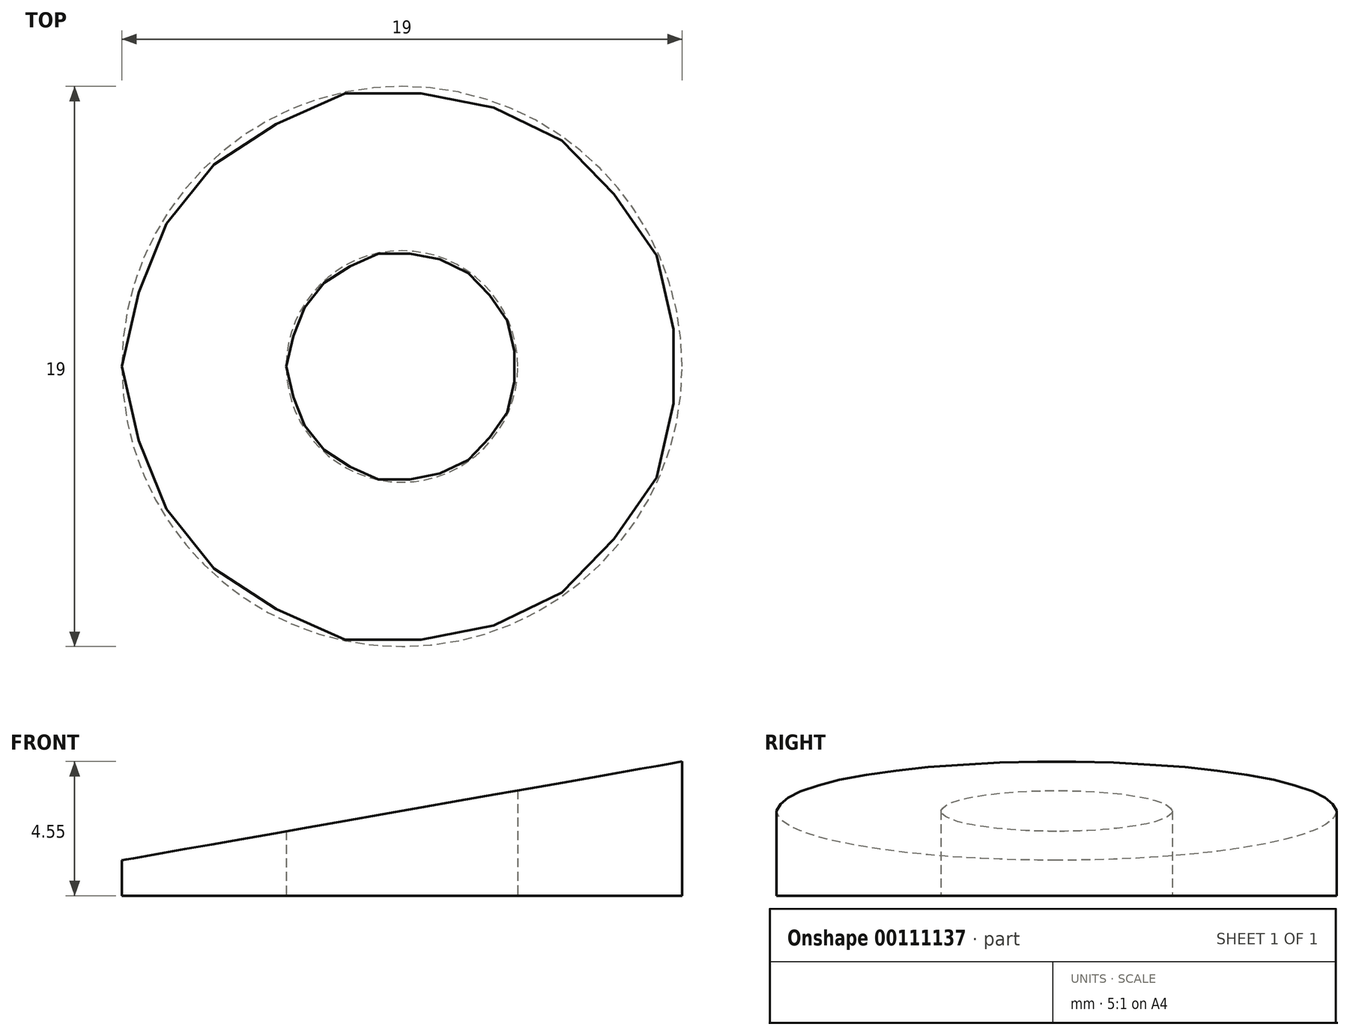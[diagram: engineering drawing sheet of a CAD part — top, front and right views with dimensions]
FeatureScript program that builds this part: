
annotation { "Feature Type Name" : "Feature", "Feature Type Description" : "" }
export const myFeature = defineFeature(function(context is Context, id is Id, definition is map)
    precondition{}
    {
        {
            var Q0;
            Q0=qCreatedBy(makeId("Top.planeOp"),FACE);
            var sketch = newSketch(context, id + "F0", { "sketchPlane" : qUnion([Q0])});
            skCircle(sketch, "E0", {"center": v(0, 0) * mm, "radius": 3.93 * mm});
            skCircle(sketch, "E1", {"center": v(0, 0) * mm, "radius": 9.5 * mm});
            skSolve(sketch);
        }
        {
            var Q0;
            Q0 = qSketchRegion(id + "F0", true);
            extrude(context, id + "F1", {"entities" : qUnion([Q0]), "depth" : 6 * mm, "offsetDistance" : 25 * mm});
        }
        {
            var Q0;
            Q0=qCreatedBy(makeId("Front.planeOp"),FACE);
            var sketch = newSketch(context, id + "F2", { "sketchPlane" : qUnion([Q0])});
            skLineSegment(sketch, "E2.0", {"start": v(-9.5, 0) * mm, "end": v(9.5, 0) * mm});
            skLineSegment(sketch, "E3.0", {"start": v(-9.5, 6) * mm, "end": v(9.5, 6) * mm, "construction": true});
            skLineSegment(sketch, "E4", {"start": v(-9.5, 0) * mm, "end": v(-9.5, 6) * mm, "construction": true});
            skLineSegment(sketch, "E5", {"start": v(9.5, 6) * mm, "end": v(9.5, 0) * mm});
            skLineSegment(sketch, "E6", {"start": v(-9.5, 1.2) * mm, "end": v(9.5, 4.55) * mm});
            skLineSegment(sketch, "E7", {"start": v(-9.5, 1.2) * mm, "end": v(-9.5, 0) * mm});
            skSolve(sketch);
        }
        {
            var Q0;
            {var subQ0=sQuery(id+"F2.wireOp",EDGE,"E2.0");Q0=makeQuery(id+"F2.imprint","IMPRINT",FACE,{"disambiguationData":[TD([[makeQuery(id+"F2.imprint","IMPRINT",EDGE,{"derivedFrom":subQ0}),1.0]])]});}
            extrude(context, id + "F3", {"entities" : qUnion([Q0]), "operationType" : NewBodyOperationType.INTERSECT, "depth" : 50 * mm, "offsetDistance" : 25 * mm, "symmetric" : true});
        }
    });
